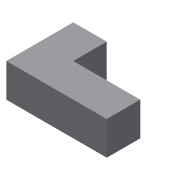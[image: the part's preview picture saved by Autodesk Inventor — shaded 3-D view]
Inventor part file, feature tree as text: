
AUTODESK INVENTOR PART (.ipt)
format: ipt  version: 2015 (Build 190159000, 159)  size: 70,656 bytes
history: native  units: in
note: dims shown in document units (in); Inventor stores cm internally (conversion verified against a paired STEP export)
features: extrude x1, sketch x1
ambient origin geometry x8: Origin, YZ Plane, XZ Plane, XY Plane, X Axis, Y Axis, Z Axis, Center Point
bodies: Solid1 (feature_tree)
feature tree (2):
  extrude  "Extrusion1"  Depth=2.0in
  sketch  "Sketch1"  dims[d0=3.0in d1=2.0in d2=1.0in d3=1.0in d4=1.0in d5=0.0in]
